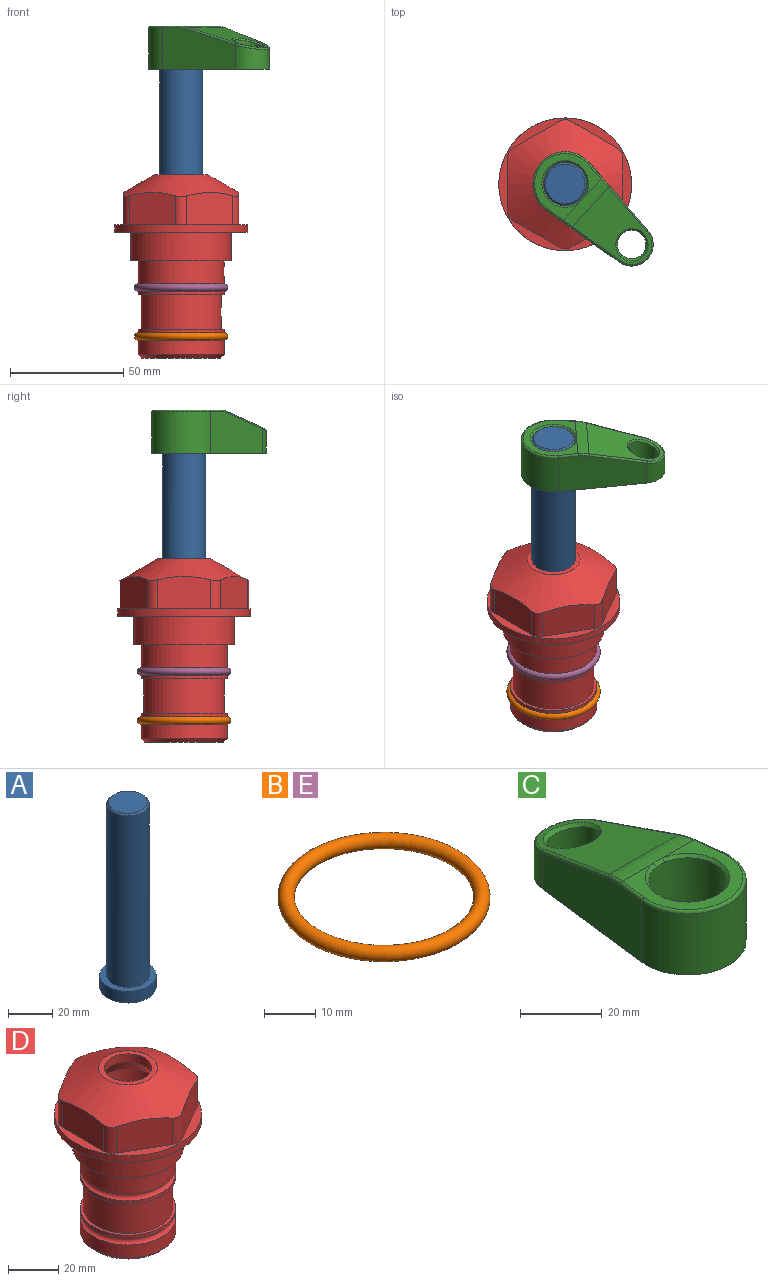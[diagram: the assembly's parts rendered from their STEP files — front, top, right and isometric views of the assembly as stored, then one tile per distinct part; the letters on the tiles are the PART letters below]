
ASSEMBLY  parts=5 mates=4
PART A: 6 faces, bbox 25.4x25.4x101.6 mm
  f0: plane 17.46x17.46mm, normal (0,0,1), area 239.5mm2, adj f5
  f1: plane 25.4x25.4mm, normal (0,0,-1), area 506.7mm2, adj f2
  f2: cylinder r=12.7mm len=25.4mm, axis (0,0,1), area 506.7mm2, adj f1,f3
  f3: plane 25.4x25.4mm, normal (0,0,1), area 221.7mm2, adj f2,f4
  f4: cylinder r=9.53mm len=94.46mm, axis (0,0,1), area 5653mm2, adj f3,f5
  f5: cone r=8.73mm half-angle=45deg, axis (0,0,-1), area 64.4mm2, adj f0,f4
PART B: 1 faces, bbox 44.7x44.7x3.2 mm
  f0: torus R=19.05mm, axis (0,0,1), area 1193.9mm2
PART C: 31 faces, bbox 31.7x65.5x19.8 mm
  f0: plane 39.12x18.26mm, normal (0.99,0.12,0), area 612.2mm2, adj f1,f4,f7,f11,f13,f15
  f1: cylinder r=9.53mm len=18.91mm, axis (0,0,-1), area 296.1mm2, adj f0,f2,f7,f17
  f2: plane 39.12x18.26mm, normal (-0.99,0.12,0), area 612.2mm2, adj f1,f4,f7,f12,f14,f16
  f3: cylinder r=6.35mm len=12.7mm, axis (0,0,-1), area 362.4mm2, adj f7,f18
  f4: cylinder r=14.29mm len=28.58mm, axis (0,0,-1), area 882.2mm2, adj f0,f2,f7,f10
  f5: cylinder r=9.53mm len=19.05mm, axis (0,0,-1), area 1092.6mm2, adj f7,f19,f20
  f6: plane 26.99x23.69mm, normal (0,0,1), area 216.2mm2, adj f9,f10,f11,f12,f19
  f7: plane 63.5x28.58mm, normal (0,0,-1), area 661.8mm2, adj f0,f1,f2,f3,f4,f5,f22,f23
  f8: plane 33.52x23.6mm, normal (0,0.26,0.97), area 486mm2, adj f9,f15,f16,f17,f18
  f9: cylinder r=19.05mm len=24.72mm, axis (1,0,0), area 120.4mm2, adj f6,f8,f13,f14,f20
  f10: torus R=13.49mm, axis (0,0,1), area 59mm2, adj f4,f6,f11,f12
  f11: cylinder r=0.79mm len=8.67mm, axis (0.12,-0.99,0), area 10.8mm2, adj f0,f6,f10,f13
  f12: cylinder r=0.79mm len=8.67mm, axis (0.12,0.99,0), area 10.8mm2, adj f2,f6,f10,f14
  f13: bspline ~4.95x1.42mm, area 6.1mm2, adj f0,f9,f11,f15
  f14: bspline ~4.95x1.42mm, area 6.1mm2, adj f2,f9,f12,f16
  f15: cylinder r=0.79mm len=25.95mm, axis (0.12,-0.96,0.26), area 32.9mm2, adj f0,f8,f13,f17
  f16: cylinder r=0.79mm len=25.95mm, axis (0.12,0.96,-0.26), area 32.9mm2, adj f2,f8,f14,f17
  f17: bspline ~18.91x8.38mm, area 30mm2, adj f1,f8,f15,f16
  f18: bspline ~14.29x14.29mm, area 48.3mm2, adj f3,f8
  f19: cone r=9.53mm half-angle=45deg, axis (0,0,1), area 66.5mm2, adj f5,f6,f20
  f20: bspline ~3.22x0.96mm, area 3.5mm2, adj f5,f9,f19
  f21: plane 2.75x2.72mm, normal (0,0,-1), area 2.9mm2, adj f23,f25,f28
  f22: plane 23.05x15.88mm, normal (-0.99,-0.12,0), area 323.6mm2, adj f7,f25,f26,f27,f28,f29
  f23: plane 23.05x15.88mm, normal (0.99,-0.12,0), area 323.6mm2, adj f7,f21,f25,f27,f28,f30
  f24: cylinder r=9.53mm len=10.69mm, axis (0,0,-1), area 114.7mm2, adj f7,f27,f29,f30
  f25: cylinder r=12.7mm len=20.59mm, axis (0,0,-1), area 381.1mm2, adj f7,f21,f22,f23,f26,f28
  f26: plane 2.75x2.72mm, normal (0,0,-1), area 2.9mm2, adj f22,f25,f28
  f27: plane 19.72x18.37mm, normal (0,-0.26,-0.97), area 291.8mm2, adj f22,f23,f24,f28,f29,f30
  f28: cylinder r=15.88mm len=19.92mm, axis (1,0,0), area 54.8mm2, adj f21,f22,f23,f25,f26,f27
  f29: cylinder r=1.59mm len=11mm, axis (0,0,-1), area 34.7mm2, adj f7,f22,f24,f27
  f30: cylinder r=1.59mm len=11mm, axis (0,0,-1), area 34.7mm2, adj f7,f23,f24,f27
PART D: 36 faces, bbox 58.7x58.7x81 mm
  f0: cylinder r=17.78mm len=35.56mm, axis (0,0,1), area 1670.8mm2, adj f23,f24,f31
  f1: cylinder r=19.05mm len=38.1mm, axis (0,0,1), area 1191.9mm2, adj f26,f27,f30
  f2: plane 58.66x58.66mm, normal (0,0,-1), area 1150.6mm2, adj f3,f28
  f3: cylinder r=29.33mm len=58.66mm, axis (0,0,-1), area 585.1mm2, adj f2,f4
  f4: plane 58.66x58.66mm, normal (0,0,1), area 475.9mm2, adj f3,f5,f6,f7,f8,f9,f10,f11
  f5: plane 20.32x14.34mm, normal (-0.5,0.87,0), area 324.4mm2, adj f4,f15,f16,f17
  f6: plane 20.32x14.34mm, normal (0.5,0.87,0), area 324.4mm2, adj f4,f14,f15,f17
  f7: plane 23.48x14.34mm, normal (1,0,0), area 324.4mm2, adj f4,f13,f14,f17
  f8: plane 20.32x14.34mm, normal (0.5,-0.87,0), area 324.4mm2, adj f4,f12,f13,f17
  f9: plane 20.32x14.34mm, normal (-0.5,-0.87,0), area 324.4mm2, adj f4,f11,f12,f17
  f10: plane 23.48x14.34mm, normal (-1,0,0), area 324.4mm2, adj f4,f11,f16,f17
  f11: cylinder r=5.08mm len=12.85mm, axis (0,0,-1), area 67.2mm2, adj f4,f9,f10,f17
  f12: cylinder r=5.08mm len=12.85mm, axis (0,0,-1), area 67.2mm2, adj f4,f8,f9,f17
  f13: cylinder r=5.08mm len=12.85mm, axis (0,0,-1), area 67.2mm2, adj f4,f7,f8,f17
  f14: cylinder r=5.08mm len=12.85mm, axis (0,0,-1), area 67.2mm2, adj f4,f6,f7,f17
  f15: cylinder r=5.08mm len=12.85mm, axis (0,0,-1), area 67.2mm2, adj f4,f5,f6,f17
  f16: cylinder r=5.08mm len=12.85mm, axis (0,0,-1), area 67.2mm2, adj f4,f5,f10,f17
  f17: cone r=11.73mm half-angle=60deg, axis (0,0,-1), area 2071.8mm2, adj f5,f6,f7,f8,f9,f10,f11,f12
  f18: plane 23.46x23.46mm, normal (0,0,1), area 147.4mm2, adj f17,f35
  f19: plane 34.93x34.93mm, normal (0,0,-1), area 958mm2, adj f29
  f20: cylinder r=19.05mm len=38.1mm, axis (0,0,1), area 760.1mm2, adj f21,f29
  f21: torus R=19.05mm, axis (0,0,1), area 565.3mm2, adj f20,f22
  f22: cylinder r=19.05mm len=38.1mm, axis (0,0,1), area 190mm2, adj f21,f23
  f23: plane 38.1x38.1mm, normal (0,0,1), area 146.9mm2, adj f0,f22
  f24: plane 38.1x38.1mm, normal (0,0,-1), area 146.9mm2, adj f0,f25
  f25: cylinder r=19.05mm len=38.1mm, axis (0,0,1), area 190mm2, adj f24,f26
  f26: torus R=19.05mm, axis (0,0,1), area 565.3mm2, adj f1,f25
  f27: plane 44.45x44.45mm, normal (0,0,-1), area 411.7mm2, adj f1,f28
  f28: cylinder r=22.23mm len=44.45mm, axis (0,0,1), area 1773.5mm2, adj f2,f27
  f29: cone r=19.05mm half-angle=45deg, axis (0,0,1), area 257.5mm2, adj f19,f20
  f30: cylinder r=3.17mm len=6.75mm, axis (-1,0,0), area 128mm2, adj f1,f33
  f31: cylinder r=3.17mm len=6.35mm, axis (-1,0,0), area 102.5mm2, adj f0,f33
  f32: plane 25.4x25.4mm, normal (0,0,1), area 506.7mm2, adj f33
  f33: cylinder r=12.7mm len=66.42mm, axis (0,0,-1), area 5236.2mm2, adj f30,f31,f32,f34
  f34: cone r=9.53mm half-angle=30deg, axis (0,0,-1), area 443.4mm2, adj f33,f35
  f35: cylinder r=9.53mm len=19.05mm, axis (0,0,-1), area 240.9mm2, adj f18,f34
PART E: same geometry as B
PLACE A rot(axis=(0,0,-1),132.3deg) t=(0,0,27.55)mm
PLACE B t=(0,0,-21.59)mm
PLACE C rot(axis=(0,0,-1),132.3deg) t=(0,0,27.55)mm
PLACE D at identity fixed
PLACE E at identity
MATE fastened B.f0 <-> D.f0  axis (0,0,1) through (0,0,-46.1)mm
MATE fastened E.f0 <-> D.f0  axis (0,0,1) through (0,0,-24.51)mm
MATE cylindrical A.f2 <-> D.f0  axis (0,0,-1) through (0,0,-10.55)mm
MATE fastened C.f4 <-> A.f2  axis (0,0,1) through (0,0,91.05)mm
